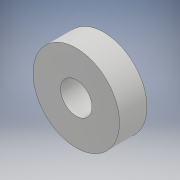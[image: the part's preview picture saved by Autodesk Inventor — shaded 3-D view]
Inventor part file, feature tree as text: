
AUTODESK INVENTOR PART (.ipt)
format: ipt  version: 2017 (Build 210142000, 142)  size: 100,352 bytes
history: native  units: mm
features: extrude x1, sketch x1
ambient origin geometry x8: Origin, YZ Plane, XZ Plane, XY Plane, X Axis, Y Axis, Z Axis, Center Point
bodies: Body1 (feature_tree)
feature tree (2):
  extrude  "Extrusion1"  Depth=7.0mm
  sketch  "Sketch2"  dims[d21=8.0mm d22=22.0mm d23=7.0mm d24=0.0mm]
